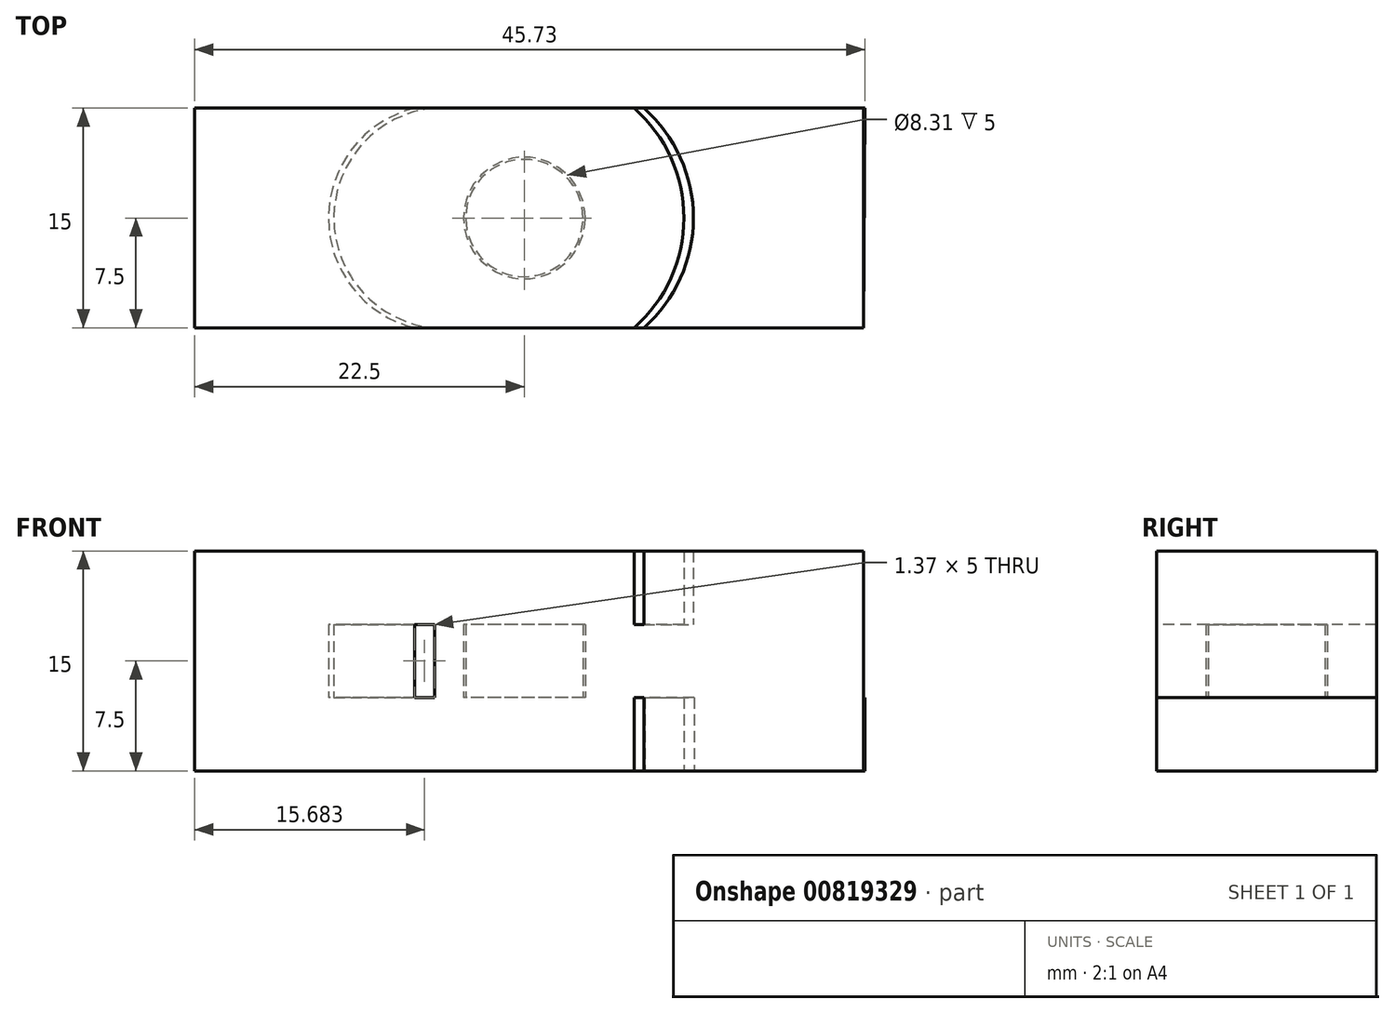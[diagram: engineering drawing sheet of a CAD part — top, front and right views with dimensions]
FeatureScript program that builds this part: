
annotation { "Feature Type Name" : "Feature", "Feature Type Description" : "" }
export const myFeature = defineFeature(function(context is Context, id is Id, definition is map)
    precondition{}
    {
        {
            var Q0;
            Q0=qCreatedBy(makeId("Top.planeOp"),FACE);
            var sketch = newSketch(context, id + "F0", { "sketchPlane" : qUnion([Q0])});
            skLineSegment(sketch, "E0.bottom", {"start": v(-15, 7.5) * mm, "end": v(15, 7.5) * mm});
            skLineSegment(sketch, "E0.top", {"start": v(-15, -7.5) * mm, "end": v(15, -7.5) * mm});
            skLineSegment(sketch, "E0.left", {"start": v(-15, 7.5) * mm, "end": v(-15, -7.5) * mm});
            skArc(sketch, "E1", {"start": v(15, -7.5) * mm, "mid": v(18.39, 0) * mm, "end": v(15, 7.5) * mm});
            skLineSegment(sketch, "E2", {"start": v(15.73, 7.5) * mm, "end": v(30.73, 7.5) * mm});
            skLineSegment(sketch, "E3", {"start": v(30.73, 7.5) * mm, "end": v(30.65, -7.5) * mm});
            skLineSegment(sketch, "E4", {"start": v(30.65, -7.5) * mm, "end": v(15.65, -7.5) * mm});
            skArc(sketch, "E5", {"start": v(15.65, -7.5) * mm, "mid": v(19.08, -0.02) * mm, "end": v(15.73, 7.5) * mm});
            skSolve(sketch);
        }
        {
            var Q0;
            Q0 = qSketchRegion(id + "F0", true);
            extrude(context, id + "F1", {"entities" : qUnion([Q0]), "depth" : 5 * mm, "offsetDistance" : 25 * mm});
        }
        {
            var Q0;
            Q0=makeQuery(id+"F1.opExtrude","CAP_FACE",FACE,{"disambiguationData":[OSD([sQuery(id+"F0.wireOp",EDGE,"E0.bottom"),sQuery(id+"F0.wireOp",EDGE,"E0.top"),sQuery(id+"F0.wireOp",EDGE,"E0.left"),sQuery(id+"F0.wireOp",EDGE,"E0.right")])],"isStart":false});
            var sketch = newSketch(context, id + "F2", { "sketchPlane" : qUnion([Q0])});
            skCircle(sketch, "E6", {"center": v(7.5, 0) * mm, "radius": 4 * mm});
            skLineSegment(sketch, "E7", {"start": v(-15, 7.5) * mm, "end": v(0, 7.5) * mm});
            skLineSegment(sketch, "E8", {"start": v(0, -7.5) * mm, "end": v(-15, -7.5) * mm});
            skLineSegment(sketch, "E9", {"start": v(-15, -7.5) * mm, "end": v(-15, 7.5) * mm});
            skLineSegment(sketch, "E10.bottom", {"start": v(1.37, -7.5) * mm, "end": v(30.65, -7.5) * mm});
            skLineSegment(sketch, "E10.top", {"start": v(1.37, 7.5) * mm, "end": v(30.65, 7.5) * mm});
            skLineSegment(sketch, "E10.right", {"start": v(30.65, -7.5) * mm, "end": v(30.65, 7.5) * mm});
            skArc(sketch, "E11", {"start": v(1.37, 7.5) * mm, "mid": v(-5.5, 0) * mm, "end": v(1.37, -7.5) * mm});
            skArc(sketch, "E12", {"start": v(0, 7.5) * mm, "mid": v(-5.87, 0) * mm, "end": v(0, -7.5) * mm});
            skCircle(sketch, "E13", {"center": v(7.5, 0) * mm, "radius": 4.15 * mm});
            skSolve(sketch);
        }
        {
            var Q0;
            Q0=makeQuery(id+"F2.imprint","IMPRINT",FACE,{"disambiguationData":[TD([[makeQuery(id+"F2.imprint","IMPRINT",EDGE,{"derivedFrom":sQuery(id+"F2.wireOp",EDGE,"E7")}),-1.0]])]});
            var Q1;
            Q1=makeQuery(id+"F2.imprint","IMPRINT",FACE,{"disambiguationData":[TD([[makeQuery(id+"F2.imprint","IMPRINT",EDGE,{"derivedFrom":sQuery(id+"F2.wireOp",EDGE,"E6")}),1.0]])]});
            extrude(context, id + "F3", {"entities" : qUnion([Q0, Q1]), "operationType" : NewBodyOperationType.ADD, "depth" : 5 * mm, "offsetDistance" : 25 * mm});
        }
        {
            var Q0;
            {var subQ0=sQuery(id+"F2.wireOp",EDGE,"E11");Q0=makeQuery(id+"F2.imprint","IMPRINT",FACE,{"disambiguationData":[TD([[makeQuery(id+"F2.imprint","IMPRINT",EDGE,{"derivedFrom":subQ0}),1.0]])]});}
            var Q1;
            {var subQ2=sQuery(id+"F2.wireOp",EDGE,"E10.right");Q1=makeQuery(id+"F2.imprint","IMPRINT",FACE,{"disambiguationData":[TD([[makeQuery(id+"F2.imprint","IMPRINT",EDGE,{"derivedFrom":subQ2}),1.0]])]});}
            extrude(context, id + "F4", {"entities" : qUnion([Q0, Q1]), "operationType" : NewBodyOperationType.ADD, "depth" : 5 * mm, "offsetDistance" : 25 * mm});
        }
        {
            var Q0;
            Q0=makeQuery(id+"F3.opExtrude","CAP_FACE",FACE,{"disambiguationData":[OSD([sQuery(id+"F2.wireOp",EDGE,"E7"),sQuery(id+"F2.wireOp",EDGE,"E8"),sQuery(id+"F2.wireOp",EDGE,"E9"),sQuery(id+"F2.wireOp",EDGE,"E12")])],"isStart":false});
            var sketch = newSketch(context, id + "F5", { "sketchPlane" : qUnion([Q0])});
            skLineSegment(sketch, "E14", {"start": v(15, 7.5) * mm, "end": v(-15, 7.5) * mm});
            skLineSegment(sketch, "E15", {"start": v(-15, 7.5) * mm, "end": v(-15, -7.5) * mm});
            skLineSegment(sketch, "E16", {"start": v(-15, -7.5) * mm, "end": v(15, -7.5) * mm});
            skArc(sketch, "E17", {"start": v(15, -7.5) * mm, "mid": v(18.39, 0) * mm, "end": v(15, 7.5) * mm});
            skLineSegment(sketch, "E18", {"start": v(15.65, 7.5) * mm, "end": v(30.65, 7.5) * mm});
            skLineSegment(sketch, "E19", {"start": v(30.65, 7.5) * mm, "end": v(30.65, -7.5) * mm});
            skLineSegment(sketch, "E20", {"start": v(30.65, -7.5) * mm, "end": v(15.65, -7.5) * mm});
            skArc(sketch, "E21", {"start": v(15.65, -7.5) * mm, "mid": v(19.04, 0) * mm, "end": v(15.65, 7.5) * mm});
            skSolve(sketch);
        }
        {
            var Q0;
            Q0=makeQuery(id+"F5.imprint","IMPRINT",FACE,{"disambiguationData":[TD([[makeQuery(id+"F5.imprint","IMPRINT",EDGE,{"derivedFrom":sQuery(id+"F5.wireOp",EDGE,"E18")}),-1.0]])]});
            extrude(context, id + "F6", {"entities" : qUnion([Q0]), "operationType" : NewBodyOperationType.ADD, "depth" : 5 * mm, "offsetDistance" : 25 * mm});
        }
        {
            var Q0;
            Q0=makeQuery(id+"F5.imprint","IMPRINT",FACE,{"disambiguationData":[TD([[makeQuery(id+"F5.imprint","IMPRINT",EDGE,{"derivedFrom":sQuery(id+"F5.wireOp",EDGE,"E14")}),1.0]])]});
            var Q1;
            {var subQ0=sQuery(id+"F5.wireOp",EDGE,"E15");Q1=makeQuery(id+"F5.imprint","IMPRINT",FACE,{"disambiguationData":[TD([[makeQuery(id+"F5.imprint","IMPRINT",EDGE,{"derivedFrom":subQ0}),1.0]])]});}
            extrude(context, id + "F7", {"entities" : qUnion([Q0, Q1]), "operationType" : NewBodyOperationType.ADD, "depth" : 5 * mm, "offsetDistance" : 25 * mm});
        }
    });
